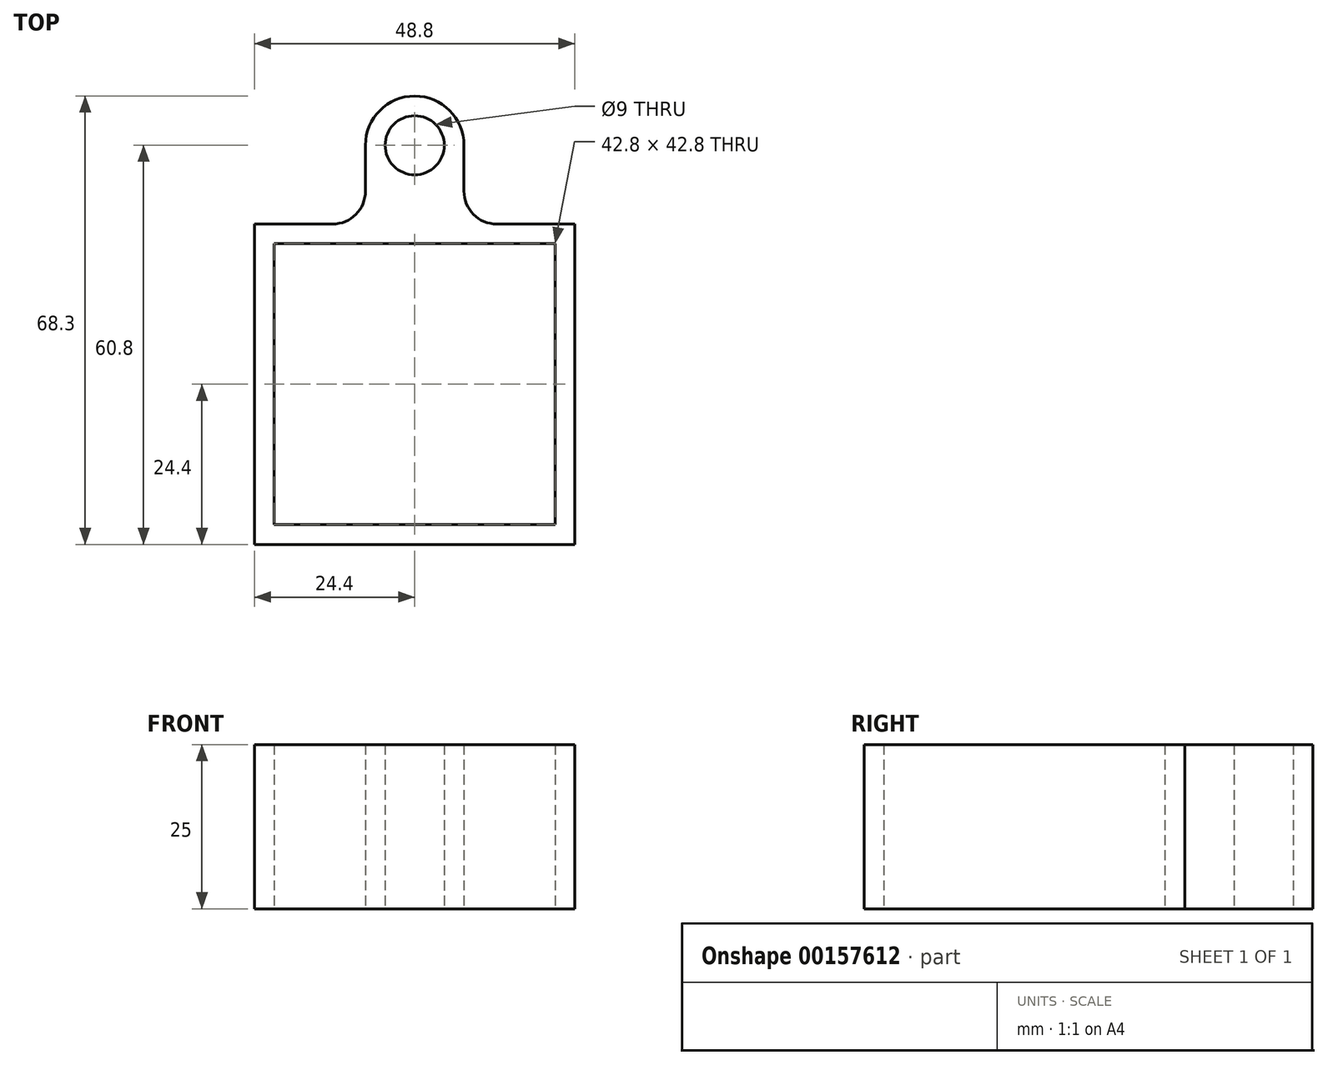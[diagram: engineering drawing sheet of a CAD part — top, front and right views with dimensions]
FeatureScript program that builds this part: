
annotation { "Feature Type Name" : "Feature", "Feature Type Description" : "" }
export const myFeature = defineFeature(function(context is Context, id is Id, definition is map)
    precondition{}
    {
        {
            var Q0;
            Q0=qCreatedBy(makeId("Top.planeOp"),FACE);
            var sketch = newSketch(context, id + "F0", { "sketchPlane" : qUnion([Q0])});
            skLineSegment(sketch, "E0.bottom", {"start": v(21.4, -21.4) * mm, "end": v(-21.4, -21.4) * mm});
            skLineSegment(sketch, "E0.top", {"start": v(21.4, 21.4) * mm, "end": v(-21.4, 21.4) * mm});
            skLineSegment(sketch, "E0.left", {"start": v(21.4, -21.4) * mm, "end": v(21.4, 21.4) * mm});
            skLineSegment(sketch, "E0.right", {"start": v(-21.4, -21.4) * mm, "end": v(-21.4, 21.4) * mm});
            skPoint(sketch, "E0.middle", {"position": v(0, 0) * mm});
            skLineSegment(sketch, "E1.0", {"start": v(24.4, 24.4) * mm, "end": v(-24.4, 24.4) * mm});
            skLineSegment(sketch, "E1.1", {"start": v(24.4, -24.4) * mm, "end": v(24.4, 24.4) * mm});
            skLineSegment(sketch, "E1.2", {"start": v(24.4, -24.4) * mm, "end": v(-24.4, -24.4) * mm});
            skLineSegment(sketch, "E1.3", {"start": v(-24.4, -24.4) * mm, "end": v(-24.4, 24.4) * mm});
            skLineSegment(sketch, "E2", {"start": v(0, 24.4) * mm, "end": v(0, 36.4) * mm, "construction": true});
            skPoint(sketch, "E2.endSnap0", {"position": v(0, 24.4) * mm});
            skCircle(sketch, "E3", {"center": v(0, 36.4) * mm, "radius": 4.5 * mm});
            skCircle(sketch, "E4.0", {"center": v(0, 36.4) * mm, "radius": 7.5 * mm});
            skLineSegment(sketch, "E5", {"start": v(0, 36.4) * mm, "end": v(-7.5, 36.4) * mm, "construction": true});
            skLineSegment(sketch, "E6", {"start": v(-7.5, 36.4) * mm, "end": v(-7.5, 24.4) * mm});
            skLineSegment(sketch, "E7.MirrorCS", {"start": v(7.5, 36.4) * mm, "end": v(7.5, 24.4) * mm});
            skSolve(sketch);
        }
        {
            var Q0;
            Q0 = qSketchRegion(id + "F0", true);
            extrude(context, id + "F1", {"entities" : qUnion([Q0]), "depth" : 25 * mm});
        }
        {
            var Q0;
            Q0=makeQuery(id+"F1.opExtrude","SWEPT_EDGE",EDGE,{"disambiguationData":[OSD([sQuery(id+"F0.wireOp",EDGE,"E1.0"),sQuery(id+"F0.wireOp",EDGE,"E7.MirrorCS")])]});
            var Q1;
            Q1=makeQuery(id+"F1.opExtrude","SWEPT_EDGE",EDGE,{"disambiguationData":[OSD([sQuery(id+"F0.wireOp",EDGE,"E1.0"),sQuery(id+"F0.wireOp",EDGE,"E6")])]});
            fillet(context, id + "F2", {"entities" : qUnion([Q0, Q1]), "radius" : 5 * mm, "tangentPropagation" : true, "allowEdgeOverflow" : false});
        }
    });
